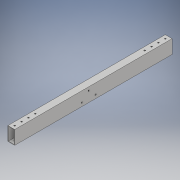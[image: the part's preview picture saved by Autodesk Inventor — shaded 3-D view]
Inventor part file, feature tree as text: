
AUTODESK INVENTOR PART (.ipt)
format: ipt  version: 2018 (Build 220112000, 112)  size: 158,720 bytes
history: native  units: in
note: dims shown in document units (in); Inventor stores cm internally (conversion verified against a paired STEP export)
features: extrude x5, sketch x5
ambient origin geometry x8: Origin, YZ Plane, XZ Plane, XY Plane, X Axis, Y Axis, Z Axis, Center Point
bodies: Solid1 (feature_tree)
feature tree (10):
  extrude  "Extrusion1"  Depth=2.0in
  extrude  "Extrusion2"  Depth=23.0in TaperAngle=0.0deg
  extrude  "Extrusion4"  Depth=0.5in
  extrude  "Extrusion5"  Depth=28.0in TaperAngle=0.0deg
  extrude  "Extrusion7"  Depth=1.0in
  sketch  "Sketch1"  dims[d0=1.0in d1=2.0in]
  sketch  "Sketch2"  dims[d2=0.0625in d3=23.0in d4=0.0in]
  sketch  "Sketch3"  dims[d5=0.5in d6=0.5in]
  sketch  "Sketch4"  dims[d7=0.2031in d8=28.0in d9=0.0in]
  sketch  "Sketch5"  dims[d10=1.0in d13=1.0in d14=2.6875in d15=0.0in d16=11.1875in d17=2.0in d18=0.5in d19=1.0in d20=1.0in d21=0.2031in d22=0.2031in d23=1.0in d24=0.0in d25=1.0in d26=1.0in d29=1.0in d30=1.0in d31=3.0625in d32=0.0in]
